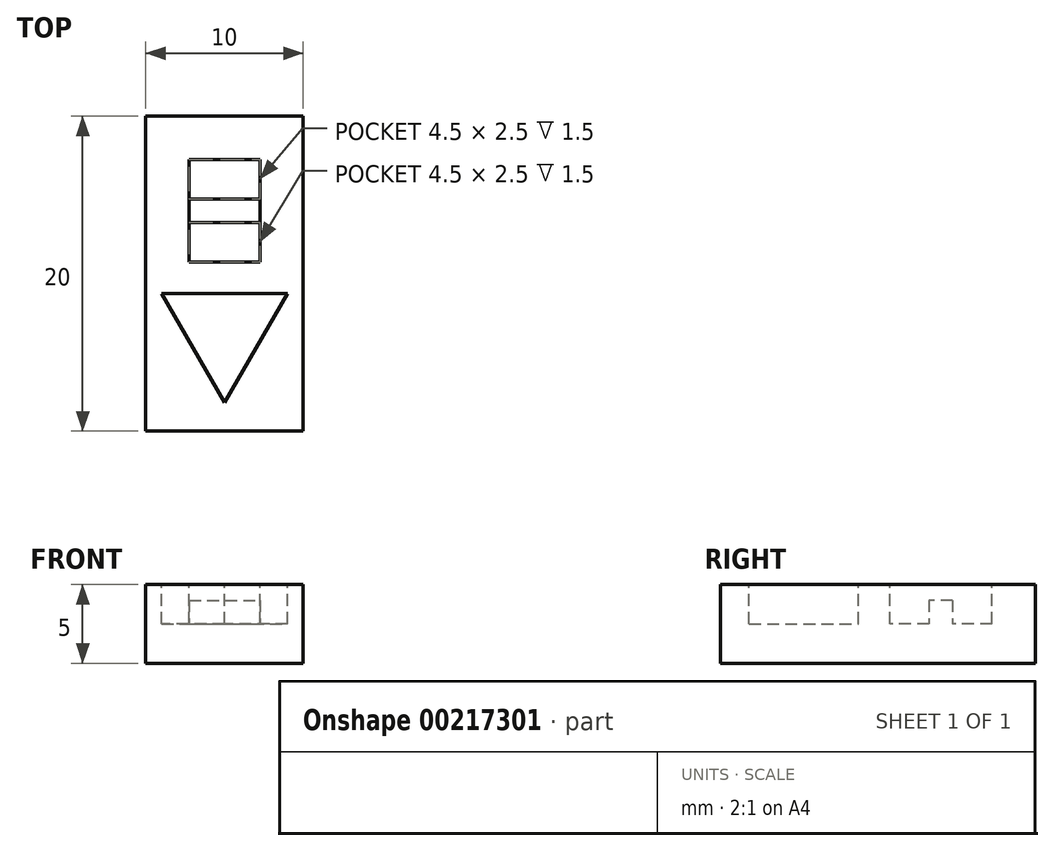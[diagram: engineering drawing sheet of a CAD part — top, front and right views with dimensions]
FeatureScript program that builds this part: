
annotation { "Feature Type Name" : "Feature", "Feature Type Description" : "" }
export const myFeature = defineFeature(function(context is Context, id is Id, definition is map)
    precondition{}
    {
        {
            var Q0;
            Q0=qCreatedBy(makeId("Top.planeOp"),FACE);
            var sketch = newSketch(context, id + "F0", { "sketchPlane" : qUnion([Q0])});
            skLineSegment(sketch, "E0.bottom", {"start": v(-5, 3.74) * mm, "end": v(5, 3.74) * mm});
            skLineSegment(sketch, "E0.top", {"start": v(-5, -6.26) * mm, "end": v(5, -6.26) * mm});
            skLineSegment(sketch, "E0.left", {"start": v(-5, 3.74) * mm, "end": v(-5, -6.26) * mm});
            skLineSegment(sketch, "E0.right", {"start": v(5, 3.74) * mm, "end": v(5, -6.26) * mm});
            skSolve(sketch);
        }
        {
            var Q0;
            Q0 = qSketchRegion(id + "F0", true);
            extrude(context, id + "F1", {"entities" : qUnion([Q0]), "depth" : 5 * mm});
        }
        {
            var Q0;
            Q0=makeQuery(id+"F1.opExtrude","CAP_FACE",FACE,{"disambiguationData":[OSD([sQuery(id+"F0.wireOp",EDGE,"E0.bottom"),sQuery(id+"F0.wireOp",EDGE,"E0.top"),sQuery(id+"F0.wireOp",EDGE,"E0.left"),sQuery(id+"F0.wireOp",EDGE,"E0.right")])],"isStart":false});
            var sketch = newSketch(context, id + "F2", { "sketchPlane" : qUnion([Q0])});
            skLineSegment(sketch, "E1.bottom", {"start": v(-2.25, 0.99) * mm, "end": v(2.25, 0.99) * mm});
            skLineSegment(sketch, "E1.top", {"start": v(-2.25, -5.51) * mm, "end": v(2.25, -5.51) * mm});
            skLineSegment(sketch, "E1.left", {"start": v(-2.25, 0.99) * mm, "end": v(-2.25, -5.51) * mm});
            skLineSegment(sketch, "E1.right", {"start": v(2.25, 0.99) * mm, "end": v(2.25, -5.51) * mm});
            skSolve(sketch);
        }
        {
            var Q0;
            Q0=makeQuery(id+"F1.opExtrude","SWEPT_FACE",FACE,{"disambiguationData":[OSD([sQuery(id+"F0.wireOp",EDGE,"E0.top")])]});
            extrude(context, id + "F3", {"entities" : qUnion([Q0]), "operationType" : NewBodyOperationType.ADD, "depth" : 10 * mm});
        }
        {
            var Q0;
            Q0=makeQuery(id+"F2.imprint","IMPRINT",FACE,{"disambiguationData":[TD([[makeQuery(id+"F2.imprint","IMPRINT",EDGE,{"derivedFrom":sQuery(id+"F2.wireOp",EDGE,"E1.bottom")}),-1.0]])]});
            extrude(context, id + "F4", {"entities" : qUnion([Q0]), "operationType" : NewBodyOperationType.REMOVE, "oppositeDirection" : true, "depth" : 2.5 * mm});
        }
        {
            var Q0;
            {var subQ0=sQuery(id+"F0.wireOp",EDGE,"E0.top");Q0=makeQuery(id+"F3.boolean.opBoolean","MERGE",FACE,{"derivedFrom":[makeQuery(id+"F1.opExtrude","CAP_FACE",FACE,{"disambiguationData":[OSD([sQuery(id+"F0.wireOp",EDGE,"E0.bottom"),subQ0,sQuery(id+"F0.wireOp",EDGE,"E0.left"),sQuery(id+"F0.wireOp",EDGE,"E0.right")])],"isStart":false}),makeQuery(id+"F3.opExtrude","SWEPT_FACE",FACE,{"disambiguationData":[OSD([subQ0]),TDD([makeQuery(id+"F1.opExtrude","CAP_EDGE",EDGE,{"disambiguationData":[OSD([subQ0])],"isStart":false})])]})]});}
            var sketch = newSketch(context, id + "F5", { "sketchPlane" : qUnion([Q0])});
            skLineSegment(sketch, "E2", {"start": v(0, -14.44) * mm, "end": v(-4, -7.51) * mm});
            skLineSegment(sketch, "E3", {"start": v(-4, -7.51) * mm, "end": v(4, -7.51) * mm});
            skLineSegment(sketch, "E4", {"start": v(4, -7.51) * mm, "end": v(0, -14.44) * mm});
            skSolve(sketch);
        }
        {
            var Q0;
            Q0=makeQuery(id+"F5.imprint","IMPRINT",FACE,{"disambiguationData":[TD([[makeQuery(id+"F5.imprint","IMPRINT",EDGE,{"derivedFrom":sQuery(id+"F5.wireOp",EDGE,"E2")}),-1.0]])]});
            extrude(context, id + "F6", {"entities" : qUnion([Q0]), "operationType" : NewBodyOperationType.REMOVE, "oppositeDirection" : true, "depth" : 2.5 * mm});
        }
        {
            var Q0;
            Q0=makeQuery(id+"F4.boolean.opBoolean","COPY",FACE,{"derivedFrom":makeQuery(id+"F4.opExtrude","CAP_FACE",FACE,{"disambiguationData":[OSD([sQuery(id+"F2.wireOp",EDGE,"E1.bottom"),sQuery(id+"F2.wireOp",EDGE,"E1.top"),sQuery(id+"F2.wireOp",EDGE,"E1.left"),sQuery(id+"F2.wireOp",EDGE,"E1.right")])],"isStart":false})});
            var sketch = newSketch(context, id + "F7", { "sketchPlane" : qUnion([Q0])});
            skLineSegment(sketch, "E5.bottom", {"start": v(-2.25, -1.51) * mm, "end": v(2.25, -1.51) * mm});
            skLineSegment(sketch, "E5.top", {"start": v(-2.25, -3.01) * mm, "end": v(2.25, -3.01) * mm});
            skLineSegment(sketch, "E5.left", {"start": v(-2.25, -1.51) * mm, "end": v(-2.25, -3.01) * mm});
            skLineSegment(sketch, "E5.right", {"start": v(2.25, -1.51) * mm, "end": v(2.25, -3.01) * mm});
            skSolve(sketch);
        }
        {
            var Q0;
            Q0=makeQuery(id+"F7.imprint","IMPRINT",FACE,{"disambiguationData":[TD([[makeQuery(id+"F7.imprint","IMPRINT",EDGE,{"derivedFrom":sQuery(id+"F7.wireOp",EDGE,"E5.bottom")}),-1.0]])]});
            extrude(context, id + "F8", {"entities" : qUnion([Q0]), "operationType" : NewBodyOperationType.ADD, "depth" : 1.5 * mm});
        }
    });
